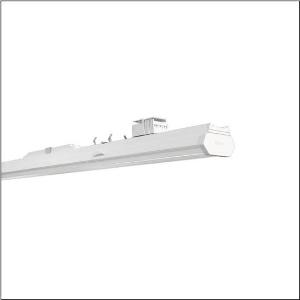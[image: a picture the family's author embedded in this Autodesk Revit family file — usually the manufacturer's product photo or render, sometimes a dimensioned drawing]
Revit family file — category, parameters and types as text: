
# Revit family: licross_r__21_protected_mo_52td12cn49xg_6de8
name_source: partatom
category: Lighting Fixtures
units: mm (PartAtom-declared; Revit-internal decimal feet)

## family parameters
Cut with Voids When Loaded = No
Host = Face
Light Source = No
Part Type = Normal
Room Calculation Point = No
Round Connector Dimension = Use Diameter
Shared = No

## types (1)
- --- (1 x LED, 9110 lm, 50.4 W, 4000K)
    Apparent Load = 50 VA
    CIE Flux Codes = 73 92 98 99 100
    Color Rendering = 80
    Color Temperature = 4000K
    Default Elevation = 1800 mm
    Description = Licross® 21 Protected MO, luminaire insert, of sheet steel, galvanised, coil coated, white, length: 1.500mm, width: 90mm, height: 103mm, LED rated luminous flux: 9.120lm, light colour: 840, SDCM (Standard Deviation of Colour Matching)MacAdam ≤ 3 SDCM (initial), control gear: ON/OFF Multilumen, CLOi, with plug, 3-pole, with phase selection, mains connection: 220..240V, AC, 50/60Hz, start of lifetime: 50W, end of service life: 61W, internal wiring halogen-free, primary light control with lens, of plastic, primary optical cover: cover, of PMMA, light emission: direct distribution, primary light characteristic: symmetric, protection rating (complete): IP54, insulation class (complete): insulation class I (protective earthing), certification: CE, ENEC, VDE, UKCA, protection symbol: D if used in an environment with non-conductive dust loads with corresponding accessories, impact resistance: IK06, permissible ambient temperature for indoor applications: -35..+45°C, corresponds to IFS (International Featured Standards) requirements for safety and quality in the food industry, reducing of maximum allowable ambient temperature of 5°C with ceiling mounting, LABS conformity tested according to VDMA 24364:2018-05, packaging unit: 1 piece
    Height = 92 mm
    Lamp = 1 x LED
    Lamp Light Flux = 9110 lm
    Lamp Power = 50.4 W
    Lamp count = 1
    Length = 1500 mm
    Luminous efficacy = 181 lm/W
    Manufacturer = Siteco
    ModVariant = No
    Model = 52TD12CN49XG
    Mounting Place = Ceiling
    Mounting Type = Pendant
    Number of Poles = 1
    OnlyDefault = Yes
    Power Factor = 1
    Product Name = Licross® 21 Protected MO
    Product group = luminaire insert | ceiling pendant
    ProductGroupID = 901
    Protection Class = Protection class I
    Protection Degree = IP 54
    RLX_Detail_Level = 1
    RLX_Emergency_Light_Flux = 0 lm
    RLX_Emergency_Type = 0
    RLX_Emergency_Type_DB = No
    RlxData = <blob elided: 22333 chars, md5=44f59fba>
    Socket = socket
    Standby Power = 0 W
    System Light Flux = 9110 lm
    System Power = 50 W
    Type Comments = factory setting: luminous flux: 100 % | (A | C | E) | 117 mA
    Type Image = l_1256148.jpg
    URL = http://relux.com
    VarID = @adj_115111
    Voltage = 0 V
    Weight = 0.00 kg
    Width = 88 mm

## geometry (parser evidence)
native form markers: Blend x4, Sweep x10
no freeform markers — native parametric forms only
